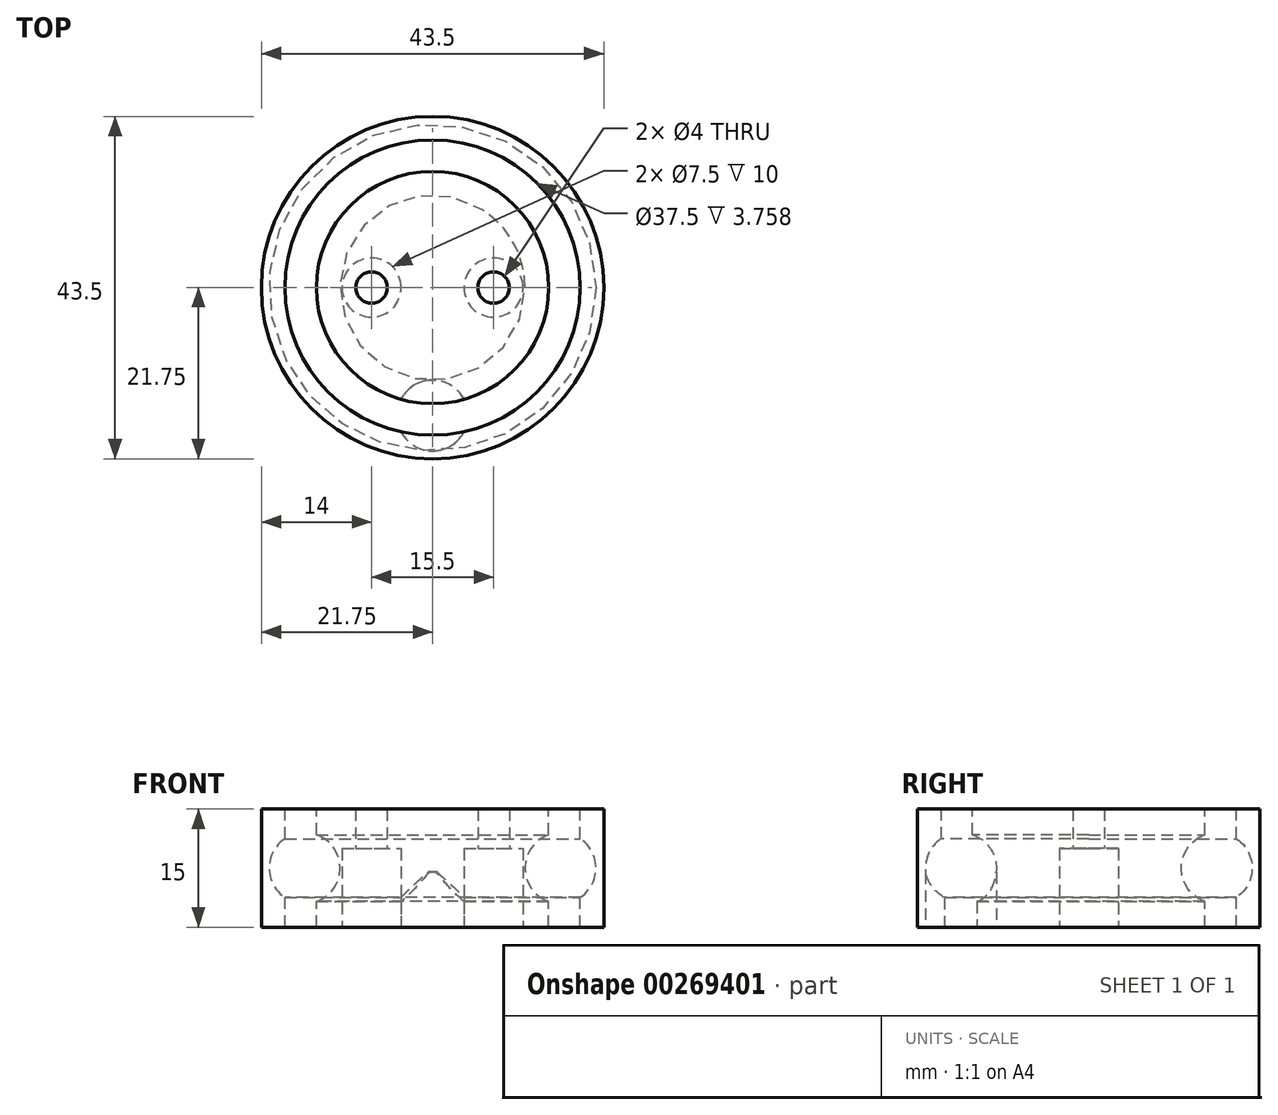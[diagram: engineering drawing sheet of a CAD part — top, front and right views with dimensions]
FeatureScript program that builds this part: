
annotation { "Feature Type Name" : "Feature", "Feature Type Description" : "" }
export const myFeature = defineFeature(function(context is Context, id is Id, definition is map)
    precondition{}
    {
        {
            var Q0;
            Q0=qCreatedBy(makeId("Top.planeOp"),FACE);
            var sketch = newSketch(context, id + "F0", { "sketchPlane" : qUnion([Q0])});
            skCircle(sketch, "E0", {"center": v(0, 0) * mm, "radius": 4 * mm});
            skCircle(sketch, "E1", {"center": v(0, 0) * mm, "radius": 21.75 * mm});
            skCircle(sketch, "E2", {"center": v(0, 0) * mm, "radius": 14.75 * mm});
            skCircle(sketch, "E3", {"center": v(0, 0) * mm, "radius": 18.75 * mm});
            skPoint(sketch, "E4", {"position": v(0, 50.94) * mm});
            skSolve(sketch);
        }
        {
            var Q0;
            Q0=makeQuery(id+"F0.imprint","IMPRINT",FACE,{"disambiguationData":[TD([[makeQuery(id+"F0.imprint","IMPRINT",EDGE,{"derivedFrom":sQuery(id+"F0.wireOp",EDGE,"E1")}),1.0]])]});
            var Q1;
            Q1=makeQuery(id+"F0.imprint","IMPRINT",FACE,{"disambiguationData":[TD([[makeQuery(id+"F0.imprint","IMPRINT",EDGE,{"derivedFrom":sQuery(id+"F0.wireOp",EDGE,"E0")}),-1.0]])]});
            var Q2;
            Q2=makeQuery(id+"F0.imprint","IMPRINT",FACE,{"disambiguationData":[TD([[makeQuery(id+"F0.imprint","IMPRINT",EDGE,{"derivedFrom":sQuery(id+"F0.wireOp",EDGE,"E0")}),1.0]])]});
            extrude(context, id + "F1", {"entities" : qUnion([Q0, Q1, Q2]), "oppositeDirection" : true, "depth" : 15 * mm});
        }
        {
            var Q0;
            Q0=qCreatedBy(makeId("Right.planeOp"),FACE);
            var sketch = newSketch(context, id + "F2", { "sketchPlane" : qUnion([Q0])});
            skLineSegment(sketch, "E5", {"start": v(0, -15) * mm, "end": v(0, 0) * mm});
            skPoint(sketch, "E6", {"position": v(0, -7.5) * mm});
            skSolve(sketch);
        }
        {
            var Q0;
            Q0=makeQuery(id+"F1.opExtrude","CAP_FACE",FACE,{"disambiguationData":[OSD([sQuery(id+"F0.wireOp",EDGE,"E0"),sQuery(id+"F0.wireOp",EDGE,"E2")])],"isStart":false});
            var sketch = newSketch(context, id + "F3", { "sketchPlane" : qUnion([Q0])});
            skPoint(sketch, "E7", {"position": v(0, -14.75) * mm});
            skPoint(sketch, "E8", {"position": v(0, -18.75) * mm});
            skSolve(sketch);
        }
        {
            var Q0;
            Q0=qCreatedBy(makeId("Right.planeOp"),FACE);
            var sketch = newSketch(context, id + "F4", { "sketchPlane" : qUnion([Q0])});
            skCircle(sketch, "E9", {"center": v(16.25, -7.5) * mm, "radius": 4.5 * mm});
            skLineSegment(sketch, "E10", {"start": v(18.75, 0) * mm, "end": v(18.75, -15) * mm});
            skSolve(sketch);
        }
        {
            var Q0;
            Q0=qCreatedBy(makeId("Right.planeOp"),FACE);
            var sketch = newSketch(context, id + "F5", { "sketchPlane" : qUnion([Q0])});
            skLineSegment(sketch, "E11", {"start": v(16.25, -3) * mm, "end": v(16.25, -12) * mm});
            skPoint(sketch, "E12", {"position": v(0, 5) * mm});
            skPoint(sketch, "E13", {"position": v(16.25, -7.5) * mm});
            skArc(sketch, "E14", {"start": v(16.25, -3) * mm, "mid": v(11.75, -7.5) * mm, "end": v(16.25, -12) * mm});
            skSolve(sketch);
        }
        {
            var Q0;
            Q0=makeQuery(id+"F4.imprint","IMPRINT",FACE,{"disambiguationData":[TD([[makeQuery(id+"F4.imprint","IMPRINT",EDGE,{"derivedFrom":sQuery(id+"F4.wireOp",EDGE,"E9")}),1.0]])]});
            var Q1;
            Q1=makeQuery(id+"F1.opExtrude","SWEPT_FACE",FACE,{"disambiguationData":[OSD([sQuery(id+"F0.wireOp",EDGE,"E2")])]});
            revolve(context, id + "F6", {"operationType" : NewBodyOperationType.REMOVE, "entities" : qUnion([Q0]), "axis" : qUnion([Q1]), "revolveType" : RevolveType.FULL, "oppositeDirection" : true});
        }
        {
            var Q0;
            Q0=qCreatedBy(makeId("Top.planeOp"),FACE);
            cPlane(context, id + "F7", {"entities" : qUnion([Q0]), "cplaneType" : CPlaneType.OFFSET, "offset" : 5 * mm, "width" : 150 * mm, "height" : 150 * mm});
        }
        {
            var Q0;
            Q0=makeQuery(id+"F1.opExtrude","CAP_FACE",FACE,{"disambiguationData":[OSD([sQuery(id+"F0.wireOp",EDGE,"E1"),sQuery(id+"F0.wireOp",EDGE,"E3")])],"isStart":false});
            var sketch = newSketch(context, id + "F8", { "sketchPlane" : qUnion([Q0])});
            skCircle(sketch, "E15", {"center": v(0, 16.25) * mm, "radius": 4.5 * mm});
            skSolve(sketch);
        }
        {
            var Q0;
            Q0=makeQuery(id+"F8.imprint","IMPRINT",FACE,{"disambiguationData":[TD([[makeQuery(id+"F8.imprint","IMPRINT",EDGE,{"derivedFrom":sQuery(id+"F8.wireOp",EDGE,"E15")}),1.0]])]});
            extrude(context, id + "F9", {"entities" : qUnion([Q0]), "operationType" : NewBodyOperationType.REMOVE, "oppositeDirection" : true, "depth" : 7 * mm});
        }
        {
            var Q0;
            Q0=makeQuery(id+"F1.opExtrude","CAP_FACE",FACE,{"disambiguationData":[OSD([sQuery(id+"F0.wireOp",EDGE,"E0"),sQuery(id+"F0.wireOp",EDGE,"E2")])],"isStart":false});
            var sketch = newSketch(context, id + "F10", { "sketchPlane" : qUnion([Q0])});
            skPoint(sketch, "E16", {"position": v(-7.75, 0) * mm});
            skPoint(sketch, "E17", {"position": v(7.75, 0) * mm});
            skCircle(sketch, "E18", {"center": v(-7.75, 0) * mm, "radius": 3.75 * mm});
            skCircle(sketch, "E19", {"center": v(7.75, 0) * mm, "radius": 3.75 * mm});
            skSolve(sketch);
        }
        {
            var Q0;
            Q0=sQuery(id+"F10.wireOp",VERTEX,"E16");
            var Q1;
            Q1=sQuery(id+"F10.wireOp",VERTEX,"E17");
            var Q2;
            Q2=makeQuery(id+"F1.opExtrude","SWEPT_BODY",BODY,{"disambiguationData":[OSD([sQuery(id+"F0.wireOp",EDGE,"E0"),sQuery(id+"F0.wireOp",EDGE,"E2")])]});
            hole(context, id + "F11", {"style" : HoleStyle.SIMPLE, "endStyle" : HoleEndStyle.THROUGH, "holeDiameter" : 4 * mm, "tappedDepth" : 12 * mm, "tapClearance" : 3, "locations" : qUnion([Q0, Q1]), "scope" : qUnion([Q2])});
        }
        {
            var Q0;
            Q0=makeQuery(id+"F10.imprint","IMPRINT",FACE,{"disambiguationData":[TD([[makeQuery(id+"F10.imprint","IMPRINT",EDGE,{"derivedFrom":sQuery(id+"F10.wireOp",EDGE,"E18")}),1.0]])]});
            var Q1;
            Q1=makeQuery(id+"F10.imprint","IMPRINT",FACE,{"disambiguationData":[TD([[makeQuery(id+"F10.imprint","IMPRINT",EDGE,{"derivedFrom":sQuery(id+"F10.wireOp",EDGE,"E19")}),1.0]])]});
            extrude(context, id + "F12", {"entities" : qUnion([Q0, Q1]), "operationType" : NewBodyOperationType.REMOVE, "oppositeDirection" : true, "depth" : 10 * mm});
        }
    });
